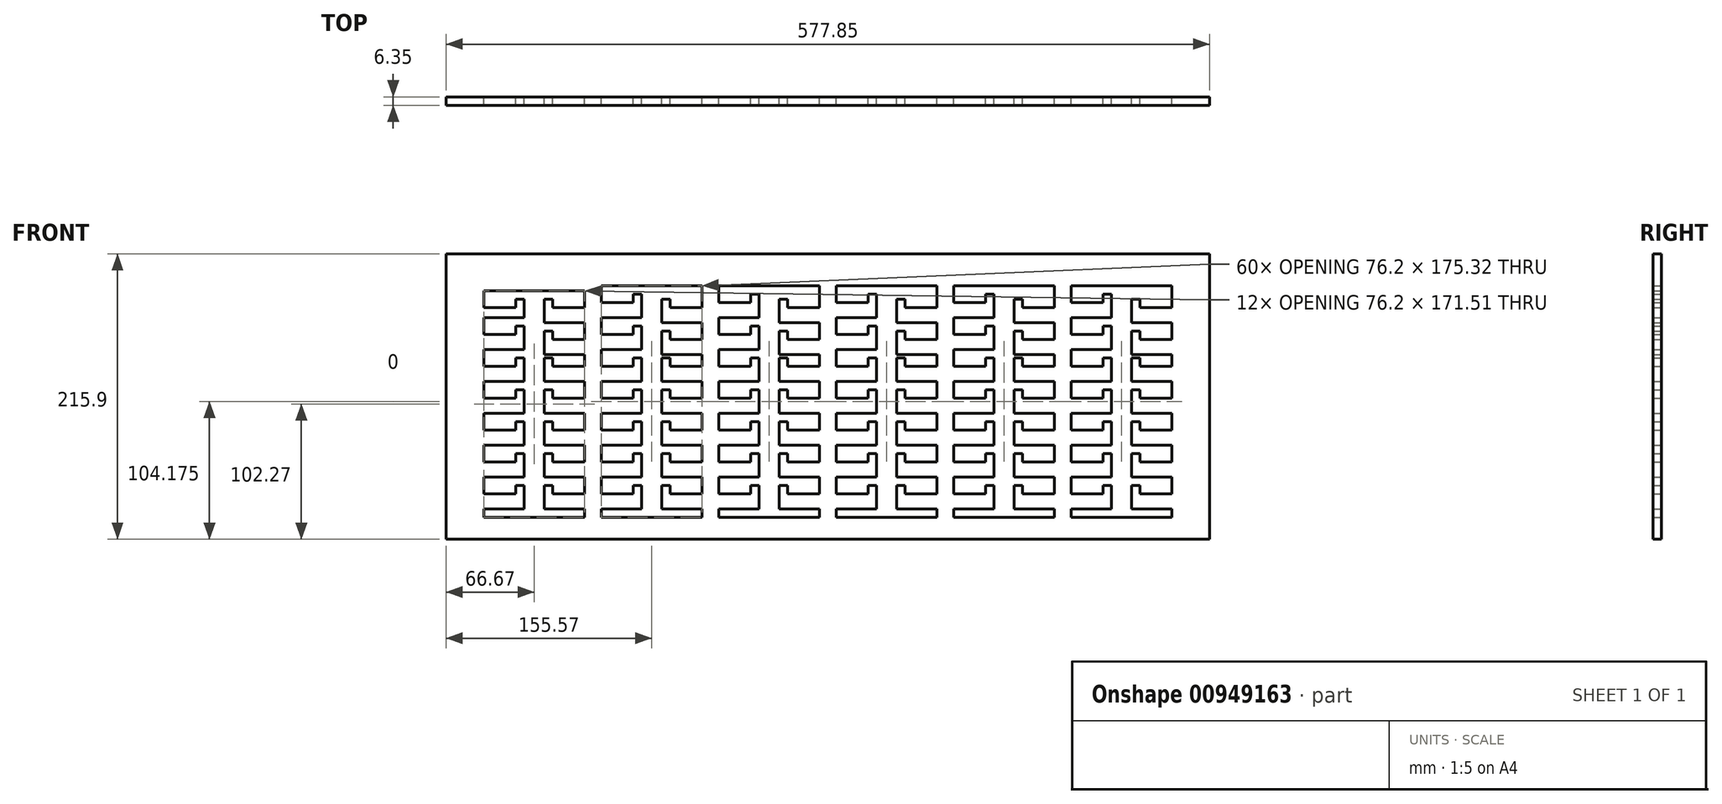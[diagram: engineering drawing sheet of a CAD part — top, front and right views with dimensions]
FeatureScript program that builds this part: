
annotation { "Feature Type Name" : "Feature", "Feature Type Description" : "" }
export const myFeature = defineFeature(function(context is Context, id is Id, definition is map)
    precondition{}
    {
        {
            var Q0;
            Q0=qCreatedBy(makeId("Front.planeOp"),FACE);
            var sketch = newSketch(context, id + "F0", { "sketchPlane" : qUnion([Q0])});
            skLineSegment(sketch, "E0", {"start": v(-97.96, -45.7) * mm, "end": v(-67.48, -45.7) * mm});
            skLineSegment(sketch, "E1", {"start": v(-67.48, -45.7) * mm, "end": v(-67.48, -27.91) * mm});
            skLineSegment(sketch, "E2", {"start": v(-67.48, -27.91) * mm, "end": v(-73.83, -27.91) * mm});
            skLineSegment(sketch, "E3", {"start": v(-73.83, -27.91) * mm, "end": v(-73.83, -34.26) * mm});
            skLineSegment(sketch, "E4", {"start": v(-73.83, -34.26) * mm, "end": v(-97.96, -34.26) * mm});
            skLineSegment(sketch, "E5", {"start": v(-97.96, -34.26) * mm, "end": v(-97.96, -21.56) * mm});
            skLineSegment(sketch, "E6", {"start": v(-97.96, -21.56) * mm, "end": v(-67.48, -21.56) * mm});
            skLineSegment(sketch, "E7", {"start": v(-67.48, -21.56) * mm, "end": v(-67.48, -3.78) * mm});
            skLineSegment(sketch, "E8", {"start": v(-67.48, -3.78) * mm, "end": v(-73.83, -3.78) * mm});
            skLineSegment(sketch, "E9", {"start": v(-73.83, -3.78) * mm, "end": v(-73.83, -10.13) * mm});
            skLineSegment(sketch, "E10", {"start": v(-73.83, -10.13) * mm, "end": v(-97.96, -10.13) * mm});
            skLineSegment(sketch, "E11", {"start": v(-97.96, -10.13) * mm, "end": v(-97.96, 2.57) * mm});
            skLineSegment(sketch, "E12", {"start": v(-97.96, 2.57) * mm, "end": v(-67.48, 2.57) * mm});
            skLineSegment(sketch, "E13", {"start": v(-67.48, 2.57) * mm, "end": v(-67.48, 20.35) * mm});
            skLineSegment(sketch, "E14", {"start": v(-67.48, 20.35) * mm, "end": v(-73.83, 20.35) * mm});
            skLineSegment(sketch, "E15", {"start": v(-73.83, 20.35) * mm, "end": v(-73.83, 14) * mm});
            skLineSegment(sketch, "E16", {"start": v(-73.83, 14) * mm, "end": v(-97.96, 14) * mm});
            skLineSegment(sketch, "E17", {"start": v(-97.96, 14) * mm, "end": v(-97.96, 26.7) * mm});
            skLineSegment(sketch, "E18", {"start": v(-97.96, 26.7) * mm, "end": v(-67.48, 26.7) * mm});
            skLineSegment(sketch, "E19", {"start": v(-67.48, 26.7) * mm, "end": v(-67.48, 44.48) * mm});
            skLineSegment(sketch, "E20", {"start": v(-67.48, 44.48) * mm, "end": v(-73.83, 44.48) * mm});
            skLineSegment(sketch, "E21", {"start": v(-73.83, 44.48) * mm, "end": v(-73.83, 38.13) * mm});
            skLineSegment(sketch, "E22", {"start": v(-73.83, 38.13) * mm, "end": v(-97.96, 38.13) * mm});
            skLineSegment(sketch, "E23", {"start": v(-97.96, 38.13) * mm, "end": v(-97.96, 50.83) * mm});
            skLineSegment(sketch, "E24", {"start": v(-21.76, -76.24) * mm, "end": v(-21.76, -69.82) * mm});
            skLineSegment(sketch, "E25", {"start": v(-21.76, -69.82) * mm, "end": v(-52.24, -69.82) * mm});
            skLineSegment(sketch, "E26", {"start": v(-52.24, -69.82) * mm, "end": v(-52.24, -52.04) * mm});
            skLineSegment(sketch, "E27", {"start": v(-52.24, -52.04) * mm, "end": v(-45.89, -52.04) * mm});
            skLineSegment(sketch, "E28", {"start": v(-45.89, -52.04) * mm, "end": v(-45.89, -58.4) * mm});
            skLineSegment(sketch, "E29", {"start": v(-45.89, -58.4) * mm, "end": v(-21.76, -58.4) * mm});
            skLineSegment(sketch, "E30", {"start": v(-21.76, -58.4) * mm, "end": v(-21.76, -45.7) * mm});
            skLineSegment(sketch, "E31", {"start": v(-21.76, -45.7) * mm, "end": v(-52.24, -45.7) * mm});
            skLineSegment(sketch, "E32", {"start": v(-52.24, -45.7) * mm, "end": v(-52.24, -27.91) * mm});
            skLineSegment(sketch, "E33", {"start": v(-52.24, -27.91) * mm, "end": v(-45.89, -27.91) * mm});
            skLineSegment(sketch, "E34", {"start": v(-45.89, -27.91) * mm, "end": v(-45.89, -34.26) * mm});
            skLineSegment(sketch, "E35", {"start": v(-45.89, -34.26) * mm, "end": v(-21.76, -34.26) * mm});
            skLineSegment(sketch, "E36", {"start": v(-21.76, -34.26) * mm, "end": v(-21.76, -21.56) * mm});
            skLineSegment(sketch, "E37", {"start": v(-21.76, -21.56) * mm, "end": v(-52.24, -21.56) * mm});
            skLineSegment(sketch, "E38", {"start": v(-52.24, -21.56) * mm, "end": v(-52.24, -3.78) * mm});
            skLineSegment(sketch, "E39", {"start": v(-52.24, -3.78) * mm, "end": v(-45.89, -3.78) * mm});
            skLineSegment(sketch, "E40", {"start": v(-45.89, -3.78) * mm, "end": v(-45.89, -10.13) * mm});
            skLineSegment(sketch, "E41", {"start": v(-45.89, -10.13) * mm, "end": v(-21.76, -10.13) * mm});
            skLineSegment(sketch, "E42", {"start": v(-21.76, -10.13) * mm, "end": v(-21.76, 2.57) * mm});
            skLineSegment(sketch, "E43", {"start": v(-21.76, 2.57) * mm, "end": v(-52.24, 2.57) * mm});
            skLineSegment(sketch, "E44", {"start": v(-52.24, 2.57) * mm, "end": v(-52.24, 20.35) * mm});
            skLineSegment(sketch, "E45", {"start": v(-52.24, 20.35) * mm, "end": v(-45.89, 20.35) * mm});
            skLineSegment(sketch, "E46", {"start": v(-45.89, 20.35) * mm, "end": v(-45.89, 14) * mm});
            skLineSegment(sketch, "E47", {"start": v(-45.89, 14) * mm, "end": v(-21.76, 14) * mm});
            skLineSegment(sketch, "E48", {"start": v(-21.76, 14) * mm, "end": v(-21.76, 26.7) * mm});
            skLineSegment(sketch, "E49", {"start": v(-21.76, 26.7) * mm, "end": v(-52.24, 26.7) * mm});
            skLineSegment(sketch, "E50", {"start": v(-52.24, 26.7) * mm, "end": v(-52.24, 44.48) * mm});
            skLineSegment(sketch, "E51", {"start": v(-52.24, 44.48) * mm, "end": v(-45.89, 44.48) * mm});
            skLineSegment(sketch, "E52", {"start": v(-45.89, 44.48) * mm, "end": v(-45.89, 38.13) * mm});
            skLineSegment(sketch, "E53", {"start": v(-45.89, 38.13) * mm, "end": v(-21.76, 38.13) * mm});
            skLineSegment(sketch, "E54", {"start": v(-21.76, 38.13) * mm, "end": v(-21.76, 50.83) * mm});
            skLineSegment(sketch, "E55", {"start": v(-67.48, -69.82) * mm, "end": v(-67.48, -52.04) * mm});
            skLineSegment(sketch, "E56", {"start": v(-73.83, -58.4) * mm, "end": v(-73.83, -52.04) * mm});
            skLineSegment(sketch, "E57", {"start": v(-73.83, -52.04) * mm, "end": v(-67.48, -52.04) * mm});
            skLineSegment(sketch, "E58", {"start": v(-67.48, -69.82) * mm, "end": v(-97.96, -69.82) * mm});
            skLineSegment(sketch, "E59", {"start": v(-97.96, -58.4) * mm, "end": v(-97.96, -45.7) * mm});
            skLineSegment(sketch, "E60", {"start": v(-97.96, -69.82) * mm, "end": v(-97.96, -76.24) * mm});
            skLineSegment(sketch, "E61", {"start": v(-97.96, -58.4) * mm, "end": v(-73.83, -58.4) * mm});
            skLineSegment(sketch, "E62", {"start": v(-97.96, -76.24) * mm, "end": v(-21.76, -76.24) * mm});
            skPoint(sketch, "E63", {"position": v(-59.86, -76.24) * mm});
            skLineSegment(sketch, "E64", {"start": v(-186.86, -45.7) * mm, "end": v(-156.38, -45.7) * mm});
            skLineSegment(sketch, "E65", {"start": v(-156.38, -45.7) * mm, "end": v(-156.38, -27.91) * mm});
            skLineSegment(sketch, "E66", {"start": v(-156.38, -27.91) * mm, "end": v(-162.73, -27.91) * mm});
            skLineSegment(sketch, "E67", {"start": v(-162.73, -27.91) * mm, "end": v(-162.73, -34.26) * mm});
            skLineSegment(sketch, "E68", {"start": v(-162.73, -34.26) * mm, "end": v(-186.86, -34.26) * mm});
            skLineSegment(sketch, "E69", {"start": v(-186.86, -34.26) * mm, "end": v(-186.86, -21.56) * mm});
            skLineSegment(sketch, "E70", {"start": v(-186.86, -21.56) * mm, "end": v(-156.38, -21.56) * mm});
            skLineSegment(sketch, "E71", {"start": v(-156.38, -21.56) * mm, "end": v(-156.38, -3.78) * mm});
            skLineSegment(sketch, "E72", {"start": v(-156.38, -3.78) * mm, "end": v(-162.73, -3.78) * mm});
            skLineSegment(sketch, "E73", {"start": v(-162.73, -3.78) * mm, "end": v(-162.73, -10.13) * mm});
            skLineSegment(sketch, "E74", {"start": v(-162.73, -10.13) * mm, "end": v(-186.86, -10.13) * mm});
            skLineSegment(sketch, "E75", {"start": v(-186.86, -10.13) * mm, "end": v(-186.86, 2.57) * mm});
            skLineSegment(sketch, "E76", {"start": v(-186.86, 2.57) * mm, "end": v(-156.38, 2.57) * mm});
            skLineSegment(sketch, "E77", {"start": v(-156.38, 2.57) * mm, "end": v(-156.38, 20.35) * mm});
            skLineSegment(sketch, "E78", {"start": v(-156.38, 20.35) * mm, "end": v(-162.73, 20.35) * mm});
            skLineSegment(sketch, "E79", {"start": v(-162.73, 20.35) * mm, "end": v(-162.73, 14) * mm});
            skLineSegment(sketch, "E80", {"start": v(-162.73, 14) * mm, "end": v(-186.86, 14) * mm});
            skLineSegment(sketch, "E81", {"start": v(-186.86, 14) * mm, "end": v(-186.86, 26.7) * mm});
            skLineSegment(sketch, "E82", {"start": v(-186.86, 26.7) * mm, "end": v(-156.38, 26.7) * mm});
            skLineSegment(sketch, "E83", {"start": v(-156.38, 26.7) * mm, "end": v(-156.38, 44.48) * mm});
            skLineSegment(sketch, "E84", {"start": v(-156.38, 44.48) * mm, "end": v(-162.73, 44.48) * mm});
            skLineSegment(sketch, "E85", {"start": v(-162.73, 44.48) * mm, "end": v(-162.73, 38.13) * mm});
            skLineSegment(sketch, "E86", {"start": v(-162.73, 38.13) * mm, "end": v(-186.86, 38.13) * mm});
            skLineSegment(sketch, "E87", {"start": v(-186.86, 38.13) * mm, "end": v(-186.86, 50.83) * mm});
            skLineSegment(sketch, "E88", {"start": v(-110.66, -76.24) * mm, "end": v(-110.66, -69.82) * mm});
            skLineSegment(sketch, "E89", {"start": v(-110.66, -69.82) * mm, "end": v(-141.14, -69.82) * mm});
            skLineSegment(sketch, "E90", {"start": v(-141.14, -69.82) * mm, "end": v(-141.14, -52.04) * mm});
            skLineSegment(sketch, "E91", {"start": v(-141.14, -52.04) * mm, "end": v(-134.79, -52.04) * mm});
            skLineSegment(sketch, "E92", {"start": v(-134.79, -52.04) * mm, "end": v(-134.79, -58.4) * mm});
            skLineSegment(sketch, "E93", {"start": v(-134.79, -58.4) * mm, "end": v(-110.66, -58.4) * mm});
            skLineSegment(sketch, "E94", {"start": v(-110.66, -58.4) * mm, "end": v(-110.66, -45.7) * mm});
            skLineSegment(sketch, "E95", {"start": v(-110.66, -45.7) * mm, "end": v(-141.14, -45.7) * mm});
            skLineSegment(sketch, "E96", {"start": v(-141.14, -45.7) * mm, "end": v(-141.14, -27.91) * mm});
            skLineSegment(sketch, "E97", {"start": v(-141.14, -27.91) * mm, "end": v(-134.79, -27.91) * mm});
            skLineSegment(sketch, "E98", {"start": v(-134.79, -27.91) * mm, "end": v(-134.79, -34.26) * mm});
            skLineSegment(sketch, "E99", {"start": v(-134.79, -34.26) * mm, "end": v(-110.66, -34.26) * mm});
            skLineSegment(sketch, "E100", {"start": v(-110.66, -34.26) * mm, "end": v(-110.66, -21.56) * mm});
            skLineSegment(sketch, "E101", {"start": v(-110.66, -21.56) * mm, "end": v(-141.14, -21.56) * mm});
            skLineSegment(sketch, "E102", {"start": v(-141.14, -21.56) * mm, "end": v(-141.14, -3.78) * mm});
            skLineSegment(sketch, "E103", {"start": v(-141.14, -3.78) * mm, "end": v(-134.79, -3.78) * mm});
            skLineSegment(sketch, "E104", {"start": v(-134.79, -3.78) * mm, "end": v(-134.79, -10.13) * mm});
            skLineSegment(sketch, "E105", {"start": v(-134.79, -10.13) * mm, "end": v(-110.66, -10.13) * mm});
            skLineSegment(sketch, "E106", {"start": v(-110.66, -10.13) * mm, "end": v(-110.66, 2.57) * mm});
            skLineSegment(sketch, "E107", {"start": v(-110.66, 2.57) * mm, "end": v(-141.14, 2.57) * mm});
            skLineSegment(sketch, "E108", {"start": v(-141.14, 2.57) * mm, "end": v(-141.14, 20.35) * mm});
            skLineSegment(sketch, "E109", {"start": v(-141.14, 20.35) * mm, "end": v(-134.79, 20.35) * mm});
            skLineSegment(sketch, "E110", {"start": v(-134.79, 20.35) * mm, "end": v(-134.79, 14) * mm});
            skLineSegment(sketch, "E111", {"start": v(-134.79, 14) * mm, "end": v(-110.66, 14) * mm});
            skLineSegment(sketch, "E112", {"start": v(-110.66, 14) * mm, "end": v(-110.66, 26.7) * mm});
            skLineSegment(sketch, "E113", {"start": v(-110.66, 26.7) * mm, "end": v(-141.14, 26.7) * mm});
            skLineSegment(sketch, "E114", {"start": v(-141.14, 26.7) * mm, "end": v(-141.14, 44.48) * mm});
            skLineSegment(sketch, "E115", {"start": v(-141.14, 44.48) * mm, "end": v(-134.79, 44.48) * mm});
            skLineSegment(sketch, "E116", {"start": v(-134.79, 44.48) * mm, "end": v(-134.79, 38.13) * mm});
            skLineSegment(sketch, "E117", {"start": v(-134.79, 38.13) * mm, "end": v(-110.66, 38.13) * mm});
            skLineSegment(sketch, "E118", {"start": v(-110.66, 38.13) * mm, "end": v(-110.66, 50.83) * mm});
            skLineSegment(sketch, "E119", {"start": v(-156.38, -69.82) * mm, "end": v(-156.38, -52.04) * mm});
            skLineSegment(sketch, "E120", {"start": v(-162.73, -58.4) * mm, "end": v(-162.73, -52.04) * mm});
            skLineSegment(sketch, "E121", {"start": v(-162.73, -52.04) * mm, "end": v(-156.38, -52.04) * mm});
            skLineSegment(sketch, "E122", {"start": v(-156.38, -69.82) * mm, "end": v(-186.86, -69.82) * mm});
            skLineSegment(sketch, "E123", {"start": v(-186.86, -58.4) * mm, "end": v(-186.86, -45.7) * mm});
            skLineSegment(sketch, "E124", {"start": v(-186.86, -69.82) * mm, "end": v(-186.86, -76.24) * mm});
            skLineSegment(sketch, "E125", {"start": v(-186.86, -58.4) * mm, "end": v(-162.73, -58.4) * mm});
            skLineSegment(sketch, "E126", {"start": v(-186.86, -76.24) * mm, "end": v(-110.66, -76.24) * mm});
            skPoint(sketch, "E127", {"position": v(-148.76, -76.24) * mm});
            skLineSegment(sketch, "E128", {"start": v(-275.76, -45.7) * mm, "end": v(-245.28, -45.7) * mm});
            skLineSegment(sketch, "E129", {"start": v(-245.28, -45.7) * mm, "end": v(-245.28, -27.91) * mm});
            skLineSegment(sketch, "E130", {"start": v(-245.28, -27.91) * mm, "end": v(-251.63, -27.91) * mm});
            skLineSegment(sketch, "E131", {"start": v(-251.63, -27.91) * mm, "end": v(-251.63, -34.26) * mm});
            skLineSegment(sketch, "E132", {"start": v(-251.63, -34.26) * mm, "end": v(-275.76, -34.26) * mm});
            skLineSegment(sketch, "E133", {"start": v(-275.76, -34.26) * mm, "end": v(-275.76, -21.56) * mm});
            skLineSegment(sketch, "E134", {"start": v(-275.76, -21.56) * mm, "end": v(-245.28, -21.56) * mm});
            skLineSegment(sketch, "E135", {"start": v(-245.28, -21.56) * mm, "end": v(-245.28, -3.78) * mm});
            skLineSegment(sketch, "E136", {"start": v(-245.28, -3.78) * mm, "end": v(-251.63, -3.78) * mm});
            skLineSegment(sketch, "E137", {"start": v(-251.63, -3.78) * mm, "end": v(-251.63, -10.13) * mm});
            skLineSegment(sketch, "E138", {"start": v(-251.63, -10.13) * mm, "end": v(-275.76, -10.13) * mm});
            skLineSegment(sketch, "E139", {"start": v(-275.76, -10.13) * mm, "end": v(-275.76, 2.57) * mm});
            skLineSegment(sketch, "E140", {"start": v(-275.76, 2.57) * mm, "end": v(-245.28, 2.57) * mm});
            skLineSegment(sketch, "E141", {"start": v(-245.28, 2.57) * mm, "end": v(-245.28, 20.35) * mm});
            skLineSegment(sketch, "E142", {"start": v(-245.28, 20.35) * mm, "end": v(-251.63, 20.35) * mm});
            skLineSegment(sketch, "E143", {"start": v(-251.63, 20.35) * mm, "end": v(-251.63, 14) * mm});
            skLineSegment(sketch, "E144", {"start": v(-251.63, 14) * mm, "end": v(-275.76, 14) * mm});
            skLineSegment(sketch, "E145", {"start": v(-275.76, 14) * mm, "end": v(-275.76, 26.7) * mm});
            skLineSegment(sketch, "E146", {"start": v(-275.76, 26.7) * mm, "end": v(-245.28, 26.7) * mm});
            skLineSegment(sketch, "E147", {"start": v(-245.28, 26.7) * mm, "end": v(-245.28, 44.48) * mm});
            skLineSegment(sketch, "E148", {"start": v(-245.28, 44.48) * mm, "end": v(-251.63, 44.48) * mm});
            skLineSegment(sketch, "E149", {"start": v(-251.63, 44.48) * mm, "end": v(-251.63, 38.13) * mm});
            skLineSegment(sketch, "E150", {"start": v(-251.63, 38.13) * mm, "end": v(-275.76, 38.13) * mm});
            skLineSegment(sketch, "E151", {"start": v(-275.76, 38.13) * mm, "end": v(-275.76, 50.83) * mm});
            skLineSegment(sketch, "E152", {"start": v(-199.56, -76.24) * mm, "end": v(-199.56, -69.82) * mm});
            skLineSegment(sketch, "E153", {"start": v(-199.56, -69.82) * mm, "end": v(-230.04, -69.82) * mm});
            skLineSegment(sketch, "E154", {"start": v(-230.04, -69.82) * mm, "end": v(-230.04, -52.04) * mm});
            skLineSegment(sketch, "E155", {"start": v(-230.04, -52.04) * mm, "end": v(-223.69, -52.04) * mm});
            skLineSegment(sketch, "E156", {"start": v(-223.69, -52.04) * mm, "end": v(-223.69, -58.4) * mm});
            skLineSegment(sketch, "E157", {"start": v(-223.69, -58.4) * mm, "end": v(-199.56, -58.4) * mm});
            skLineSegment(sketch, "E158", {"start": v(-199.56, -58.4) * mm, "end": v(-199.56, -45.7) * mm});
            skLineSegment(sketch, "E159", {"start": v(-199.56, -45.7) * mm, "end": v(-230.04, -45.7) * mm});
            skLineSegment(sketch, "E160", {"start": v(-230.04, -45.7) * mm, "end": v(-230.04, -27.91) * mm});
            skLineSegment(sketch, "E161", {"start": v(-230.04, -27.91) * mm, "end": v(-223.69, -27.91) * mm});
            skLineSegment(sketch, "E162", {"start": v(-223.69, -27.91) * mm, "end": v(-223.69, -34.26) * mm});
            skLineSegment(sketch, "E163", {"start": v(-223.69, -34.26) * mm, "end": v(-199.56, -34.26) * mm});
            skLineSegment(sketch, "E164", {"start": v(-199.56, -34.26) * mm, "end": v(-199.56, -21.56) * mm});
            skLineSegment(sketch, "E165", {"start": v(-199.56, -21.56) * mm, "end": v(-230.04, -21.56) * mm});
            skLineSegment(sketch, "E166", {"start": v(-230.04, -21.56) * mm, "end": v(-230.04, -3.78) * mm});
            skLineSegment(sketch, "E167", {"start": v(-230.04, -3.78) * mm, "end": v(-223.69, -3.78) * mm});
            skLineSegment(sketch, "E168", {"start": v(-223.69, -3.78) * mm, "end": v(-223.69, -10.13) * mm});
            skLineSegment(sketch, "E169", {"start": v(-223.69, -10.13) * mm, "end": v(-199.56, -10.13) * mm});
            skLineSegment(sketch, "E170", {"start": v(-199.56, -10.13) * mm, "end": v(-199.56, 2.57) * mm});
            skLineSegment(sketch, "E171", {"start": v(-199.56, 2.57) * mm, "end": v(-230.04, 2.57) * mm});
            skLineSegment(sketch, "E172", {"start": v(-230.04, 2.57) * mm, "end": v(-230.04, 20.35) * mm});
            skLineSegment(sketch, "E173", {"start": v(-230.04, 20.35) * mm, "end": v(-223.69, 20.35) * mm});
            skLineSegment(sketch, "E174", {"start": v(-223.69, 20.35) * mm, "end": v(-223.69, 14) * mm});
            skLineSegment(sketch, "E175", {"start": v(-223.69, 14) * mm, "end": v(-199.56, 14) * mm});
            skLineSegment(sketch, "E176", {"start": v(-199.56, 14) * mm, "end": v(-199.56, 26.7) * mm});
            skLineSegment(sketch, "E177", {"start": v(-199.56, 26.7) * mm, "end": v(-230.04, 26.7) * mm});
            skLineSegment(sketch, "E178", {"start": v(-230.04, 26.7) * mm, "end": v(-230.04, 44.48) * mm});
            skLineSegment(sketch, "E179", {"start": v(-230.04, 44.48) * mm, "end": v(-223.69, 44.48) * mm});
            skLineSegment(sketch, "E180", {"start": v(-223.69, 44.48) * mm, "end": v(-223.69, 38.13) * mm});
            skLineSegment(sketch, "E181", {"start": v(-223.69, 38.13) * mm, "end": v(-199.56, 38.13) * mm});
            skLineSegment(sketch, "E182", {"start": v(-199.56, 38.13) * mm, "end": v(-199.56, 50.83) * mm});
            skLineSegment(sketch, "E183", {"start": v(-245.28, -69.82) * mm, "end": v(-245.28, -52.04) * mm});
            skLineSegment(sketch, "E184", {"start": v(-251.63, -58.4) * mm, "end": v(-251.63, -52.04) * mm});
            skLineSegment(sketch, "E185", {"start": v(-251.63, -52.04) * mm, "end": v(-245.28, -52.04) * mm});
            skLineSegment(sketch, "E186", {"start": v(-245.28, -69.82) * mm, "end": v(-275.76, -69.82) * mm});
            skLineSegment(sketch, "E187", {"start": v(-275.76, -58.4) * mm, "end": v(-275.76, -45.7) * mm});
            skLineSegment(sketch, "E188", {"start": v(-275.76, -69.82) * mm, "end": v(-275.76, -76.24) * mm});
            skLineSegment(sketch, "E189", {"start": v(-275.76, -58.4) * mm, "end": v(-251.63, -58.4) * mm});
            skLineSegment(sketch, "E190", {"start": v(-275.76, -76.24) * mm, "end": v(-199.56, -76.24) * mm});
            skPoint(sketch, "E191", {"position": v(-237.66, -76.24) * mm});
            skLineSegment(sketch, "E192", {"start": v(-364.66, -45.7) * mm, "end": v(-334.18, -45.7) * mm});
            skLineSegment(sketch, "E193", {"start": v(-334.18, -45.7) * mm, "end": v(-334.18, -27.91) * mm});
            skLineSegment(sketch, "E194", {"start": v(-334.18, -27.91) * mm, "end": v(-340.53, -27.91) * mm});
            skLineSegment(sketch, "E195", {"start": v(-340.53, -27.91) * mm, "end": v(-340.53, -34.26) * mm});
            skLineSegment(sketch, "E196", {"start": v(-340.53, -34.26) * mm, "end": v(-364.66, -34.26) * mm});
            skLineSegment(sketch, "E197", {"start": v(-364.66, -34.26) * mm, "end": v(-364.66, -21.56) * mm});
            skLineSegment(sketch, "E198", {"start": v(-364.66, -21.56) * mm, "end": v(-334.18, -21.56) * mm});
            skLineSegment(sketch, "E199", {"start": v(-334.18, -21.56) * mm, "end": v(-334.18, -3.78) * mm});
            skLineSegment(sketch, "E200", {"start": v(-334.18, -3.78) * mm, "end": v(-340.53, -3.78) * mm});
            skLineSegment(sketch, "E201", {"start": v(-340.53, -3.78) * mm, "end": v(-340.53, -10.13) * mm});
            skLineSegment(sketch, "E202", {"start": v(-340.53, -10.13) * mm, "end": v(-364.66, -10.13) * mm});
            skLineSegment(sketch, "E203", {"start": v(-364.66, -10.13) * mm, "end": v(-364.66, 2.57) * mm});
            skLineSegment(sketch, "E204", {"start": v(-364.66, 2.57) * mm, "end": v(-334.18, 2.57) * mm});
            skLineSegment(sketch, "E205", {"start": v(-334.18, 2.57) * mm, "end": v(-334.18, 20.35) * mm});
            skLineSegment(sketch, "E206", {"start": v(-334.18, 20.35) * mm, "end": v(-340.53, 20.35) * mm});
            skLineSegment(sketch, "E207", {"start": v(-340.53, 20.35) * mm, "end": v(-340.53, 14) * mm});
            skLineSegment(sketch, "E208", {"start": v(-340.53, 14) * mm, "end": v(-364.66, 14) * mm});
            skLineSegment(sketch, "E209", {"start": v(-364.66, 14) * mm, "end": v(-364.66, 26.7) * mm});
            skLineSegment(sketch, "E210", {"start": v(-364.66, 26.7) * mm, "end": v(-334.18, 26.7) * mm});
            skLineSegment(sketch, "E211", {"start": v(-334.18, 26.7) * mm, "end": v(-334.18, 44.48) * mm});
            skLineSegment(sketch, "E212", {"start": v(-334.18, 44.48) * mm, "end": v(-340.53, 44.48) * mm});
            skLineSegment(sketch, "E213", {"start": v(-340.53, 44.48) * mm, "end": v(-340.53, 38.13) * mm});
            skLineSegment(sketch, "E214", {"start": v(-340.53, 38.13) * mm, "end": v(-364.66, 38.13) * mm});
            skLineSegment(sketch, "E215", {"start": v(-364.66, 38.13) * mm, "end": v(-364.66, 50.83) * mm});
            skLineSegment(sketch, "E216", {"start": v(-288.46, -76.24) * mm, "end": v(-288.46, -69.82) * mm});
            skLineSegment(sketch, "E217", {"start": v(-288.46, -69.82) * mm, "end": v(-318.94, -69.82) * mm});
            skLineSegment(sketch, "E218", {"start": v(-318.94, -69.82) * mm, "end": v(-318.94, -52.04) * mm});
            skLineSegment(sketch, "E219", {"start": v(-318.94, -52.04) * mm, "end": v(-312.59, -52.04) * mm});
            skLineSegment(sketch, "E220", {"start": v(-312.59, -52.04) * mm, "end": v(-312.59, -58.4) * mm});
            skLineSegment(sketch, "E221", {"start": v(-312.59, -58.4) * mm, "end": v(-288.46, -58.4) * mm});
            skLineSegment(sketch, "E222", {"start": v(-288.46, -58.4) * mm, "end": v(-288.46, -45.7) * mm});
            skLineSegment(sketch, "E223", {"start": v(-288.46, -45.7) * mm, "end": v(-318.94, -45.7) * mm});
            skLineSegment(sketch, "E224", {"start": v(-318.94, -45.7) * mm, "end": v(-318.94, -27.91) * mm});
            skLineSegment(sketch, "E225", {"start": v(-318.94, -27.91) * mm, "end": v(-312.59, -27.91) * mm});
            skLineSegment(sketch, "E226", {"start": v(-312.59, -27.91) * mm, "end": v(-312.59, -34.26) * mm});
            skLineSegment(sketch, "E227", {"start": v(-312.59, -34.26) * mm, "end": v(-288.46, -34.26) * mm});
            skLineSegment(sketch, "E228", {"start": v(-288.46, -34.26) * mm, "end": v(-288.46, -21.56) * mm});
            skLineSegment(sketch, "E229", {"start": v(-288.46, -21.56) * mm, "end": v(-318.94, -21.56) * mm});
            skLineSegment(sketch, "E230", {"start": v(-318.94, -21.56) * mm, "end": v(-318.94, -3.78) * mm});
            skLineSegment(sketch, "E231", {"start": v(-318.94, -3.78) * mm, "end": v(-312.59, -3.78) * mm});
            skLineSegment(sketch, "E232", {"start": v(-312.59, -3.78) * mm, "end": v(-312.59, -10.13) * mm});
            skLineSegment(sketch, "E233", {"start": v(-312.59, -10.13) * mm, "end": v(-288.46, -10.13) * mm});
            skLineSegment(sketch, "E234", {"start": v(-288.46, -10.13) * mm, "end": v(-288.46, 2.57) * mm});
            skLineSegment(sketch, "E235", {"start": v(-288.46, 2.57) * mm, "end": v(-318.94, 2.57) * mm});
            skLineSegment(sketch, "E236", {"start": v(-318.94, 2.57) * mm, "end": v(-318.94, 20.35) * mm});
            skLineSegment(sketch, "E237", {"start": v(-318.94, 20.35) * mm, "end": v(-312.59, 20.35) * mm});
            skLineSegment(sketch, "E238", {"start": v(-312.59, 20.35) * mm, "end": v(-312.59, 14) * mm});
            skLineSegment(sketch, "E239", {"start": v(-312.59, 14) * mm, "end": v(-288.46, 14) * mm});
            skLineSegment(sketch, "E240", {"start": v(-288.46, 14) * mm, "end": v(-288.46, 26.7) * mm});
            skLineSegment(sketch, "E241", {"start": v(-288.46, 26.7) * mm, "end": v(-318.94, 26.7) * mm});
            skLineSegment(sketch, "E242", {"start": v(-318.94, 26.7) * mm, "end": v(-318.94, 44.48) * mm});
            skLineSegment(sketch, "E243", {"start": v(-318.94, 44.48) * mm, "end": v(-312.59, 44.48) * mm});
            skLineSegment(sketch, "E244", {"start": v(-312.59, 44.48) * mm, "end": v(-312.59, 38.13) * mm});
            skLineSegment(sketch, "E245", {"start": v(-312.59, 38.13) * mm, "end": v(-288.46, 38.13) * mm});
            skLineSegment(sketch, "E246", {"start": v(-288.46, 38.13) * mm, "end": v(-288.46, 50.83) * mm});
            skLineSegment(sketch, "E247", {"start": v(-334.18, -69.82) * mm, "end": v(-334.18, -52.04) * mm});
            skLineSegment(sketch, "E248", {"start": v(-340.53, -58.4) * mm, "end": v(-340.53, -52.04) * mm});
            skLineSegment(sketch, "E249", {"start": v(-340.53, -52.04) * mm, "end": v(-334.18, -52.04) * mm});
            skLineSegment(sketch, "E250", {"start": v(-334.18, -69.82) * mm, "end": v(-364.66, -69.82) * mm});
            skLineSegment(sketch, "E251", {"start": v(-364.66, -58.4) * mm, "end": v(-364.66, -45.7) * mm});
            skLineSegment(sketch, "E252", {"start": v(-364.66, -69.82) * mm, "end": v(-364.66, -76.24) * mm});
            skLineSegment(sketch, "E253", {"start": v(-364.66, -58.4) * mm, "end": v(-340.53, -58.4) * mm});
            skLineSegment(sketch, "E254", {"start": v(-364.66, -76.24) * mm, "end": v(-288.46, -76.24) * mm});
            skPoint(sketch, "E255", {"position": v(-326.56, -76.24) * mm});
            skLineSegment(sketch, "E256.bottom", {"start": v(6.82, 123.15) * mm, "end": v(-571.03, 123.15) * mm});
            skLineSegment(sketch, "E256.top", {"start": v(6.82, -92.75) * mm, "end": v(-571.03, -92.75) * mm});
            skLineSegment(sketch, "E256.left", {"start": v(6.82, 123.15) * mm, "end": v(6.82, -92.75) * mm});
            skLineSegment(sketch, "E256.right", {"start": v(-571.03, 123.15) * mm, "end": v(-571.03, -92.75) * mm});
            skPoint(sketch, "E257", {"position": v(-282.1, 123.15) * mm});
            skLineSegment(sketch, "E258", {"start": v(-453.56, -45.7) * mm, "end": v(-423.08, -45.7) * mm});
            skLineSegment(sketch, "E259", {"start": v(-423.08, -45.7) * mm, "end": v(-423.08, -27.91) * mm});
            skLineSegment(sketch, "E260", {"start": v(-423.08, -27.91) * mm, "end": v(-429.43, -27.91) * mm});
            skLineSegment(sketch, "E261", {"start": v(-429.43, -27.91) * mm, "end": v(-429.43, -34.26) * mm});
            skLineSegment(sketch, "E262", {"start": v(-429.43, -34.26) * mm, "end": v(-453.56, -34.26) * mm});
            skLineSegment(sketch, "E263", {"start": v(-453.56, -34.26) * mm, "end": v(-453.56, -21.56) * mm});
            skLineSegment(sketch, "E264", {"start": v(-453.56, -21.56) * mm, "end": v(-423.08, -21.56) * mm});
            skLineSegment(sketch, "E265", {"start": v(-423.08, -21.56) * mm, "end": v(-423.08, -3.78) * mm});
            skLineSegment(sketch, "E266", {"start": v(-423.08, -3.78) * mm, "end": v(-429.43, -3.78) * mm});
            skLineSegment(sketch, "E267", {"start": v(-429.43, -3.78) * mm, "end": v(-429.43, -10.13) * mm});
            skLineSegment(sketch, "E268", {"start": v(-429.43, -10.13) * mm, "end": v(-453.56, -10.13) * mm});
            skLineSegment(sketch, "E269", {"start": v(-453.56, -10.13) * mm, "end": v(-453.56, 2.57) * mm});
            skLineSegment(sketch, "E270", {"start": v(-453.56, 2.57) * mm, "end": v(-423.08, 2.57) * mm});
            skLineSegment(sketch, "E271", {"start": v(-423.08, 2.57) * mm, "end": v(-423.08, 20.35) * mm});
            skLineSegment(sketch, "E272", {"start": v(-423.08, 20.35) * mm, "end": v(-429.43, 20.35) * mm});
            skLineSegment(sketch, "E273", {"start": v(-429.43, 20.35) * mm, "end": v(-429.43, 14) * mm});
            skLineSegment(sketch, "E274", {"start": v(-429.43, 14) * mm, "end": v(-453.56, 14) * mm});
            skLineSegment(sketch, "E275", {"start": v(-453.56, 14) * mm, "end": v(-453.56, 26.7) * mm});
            skLineSegment(sketch, "E276", {"start": v(-453.56, 26.7) * mm, "end": v(-423.08, 26.7) * mm});
            skLineSegment(sketch, "E277", {"start": v(-423.08, 26.7) * mm, "end": v(-423.08, 44.48) * mm});
            skLineSegment(sketch, "E278", {"start": v(-423.08, 44.48) * mm, "end": v(-429.43, 44.48) * mm});
            skLineSegment(sketch, "E279", {"start": v(-429.43, 44.48) * mm, "end": v(-429.43, 38.13) * mm});
            skLineSegment(sketch, "E280", {"start": v(-429.43, 38.13) * mm, "end": v(-453.56, 38.13) * mm});
            skLineSegment(sketch, "E281", {"start": v(-453.56, 38.13) * mm, "end": v(-453.56, 50.83) * mm});
            skLineSegment(sketch, "E282", {"start": v(-377.36, -76.24) * mm, "end": v(-377.36, -69.82) * mm});
            skLineSegment(sketch, "E283", {"start": v(-377.36, -69.82) * mm, "end": v(-407.84, -69.82) * mm});
            skLineSegment(sketch, "E284", {"start": v(-407.84, -69.82) * mm, "end": v(-407.84, -52.04) * mm});
            skLineSegment(sketch, "E285", {"start": v(-407.84, -52.04) * mm, "end": v(-401.49, -52.04) * mm});
            skLineSegment(sketch, "E286", {"start": v(-401.49, -52.04) * mm, "end": v(-401.49, -58.4) * mm});
            skLineSegment(sketch, "E287", {"start": v(-401.49, -58.4) * mm, "end": v(-377.36, -58.4) * mm});
            skLineSegment(sketch, "E288", {"start": v(-377.36, -58.4) * mm, "end": v(-377.36, -45.7) * mm});
            skLineSegment(sketch, "E289", {"start": v(-377.36, -45.7) * mm, "end": v(-407.84, -45.7) * mm});
            skLineSegment(sketch, "E290", {"start": v(-407.84, -45.7) * mm, "end": v(-407.84, -27.91) * mm});
            skLineSegment(sketch, "E291", {"start": v(-407.84, -27.91) * mm, "end": v(-401.49, -27.91) * mm});
            skLineSegment(sketch, "E292", {"start": v(-401.49, -27.91) * mm, "end": v(-401.49, -34.26) * mm});
            skLineSegment(sketch, "E293", {"start": v(-401.49, -34.26) * mm, "end": v(-377.36, -34.26) * mm});
            skLineSegment(sketch, "E294", {"start": v(-377.36, -34.26) * mm, "end": v(-377.36, -21.56) * mm});
            skLineSegment(sketch, "E295", {"start": v(-377.36, -21.56) * mm, "end": v(-407.84, -21.56) * mm});
            skLineSegment(sketch, "E296", {"start": v(-407.84, -21.56) * mm, "end": v(-407.84, -3.78) * mm});
            skLineSegment(sketch, "E297", {"start": v(-407.84, -3.78) * mm, "end": v(-401.49, -3.78) * mm});
            skLineSegment(sketch, "E298", {"start": v(-401.49, -3.78) * mm, "end": v(-401.49, -10.13) * mm});
            skLineSegment(sketch, "E299", {"start": v(-401.49, -10.13) * mm, "end": v(-377.36, -10.13) * mm});
            skLineSegment(sketch, "E300", {"start": v(-377.36, -10.13) * mm, "end": v(-377.36, 2.57) * mm});
            skLineSegment(sketch, "E301", {"start": v(-377.36, 2.57) * mm, "end": v(-407.84, 2.57) * mm});
            skLineSegment(sketch, "E302", {"start": v(-407.84, 2.57) * mm, "end": v(-407.84, 20.35) * mm});
            skLineSegment(sketch, "E303", {"start": v(-407.84, 20.35) * mm, "end": v(-401.49, 20.35) * mm});
            skLineSegment(sketch, "E304", {"start": v(-401.49, 20.35) * mm, "end": v(-401.49, 14) * mm});
            skLineSegment(sketch, "E305", {"start": v(-401.49, 14) * mm, "end": v(-377.36, 14) * mm});
            skLineSegment(sketch, "E306", {"start": v(-377.36, 14) * mm, "end": v(-377.36, 26.7) * mm});
            skLineSegment(sketch, "E307", {"start": v(-377.36, 26.7) * mm, "end": v(-407.84, 26.7) * mm});
            skLineSegment(sketch, "E308", {"start": v(-407.84, 26.7) * mm, "end": v(-407.84, 44.48) * mm});
            skLineSegment(sketch, "E309", {"start": v(-407.84, 44.48) * mm, "end": v(-401.49, 44.48) * mm});
            skLineSegment(sketch, "E310", {"start": v(-401.49, 44.48) * mm, "end": v(-401.49, 38.13) * mm});
            skLineSegment(sketch, "E311", {"start": v(-401.49, 38.13) * mm, "end": v(-377.36, 38.13) * mm});
            skLineSegment(sketch, "E312", {"start": v(-377.36, 38.13) * mm, "end": v(-377.36, 50.83) * mm});
            skLineSegment(sketch, "E313", {"start": v(-423.08, -69.82) * mm, "end": v(-423.08, -52.04) * mm});
            skLineSegment(sketch, "E314", {"start": v(-429.43, -58.4) * mm, "end": v(-429.43, -52.04) * mm});
            skLineSegment(sketch, "E315", {"start": v(-429.43, -52.04) * mm, "end": v(-423.08, -52.04) * mm});
            skLineSegment(sketch, "E316", {"start": v(-423.08, -69.82) * mm, "end": v(-453.56, -69.82) * mm});
            skLineSegment(sketch, "E317", {"start": v(-453.56, -58.4) * mm, "end": v(-453.56, -45.7) * mm});
            skLineSegment(sketch, "E318", {"start": v(-453.56, -69.82) * mm, "end": v(-453.56, -76.24) * mm});
            skLineSegment(sketch, "E319", {"start": v(-453.56, -58.4) * mm, "end": v(-429.43, -58.4) * mm});
            skLineSegment(sketch, "E320", {"start": v(-453.56, -76.24) * mm, "end": v(-377.36, -76.24) * mm});
            skPoint(sketch, "E321", {"position": v(-415.46, -76.24) * mm});
            skLineSegment(sketch, "E322", {"start": v(-542.46, -45.7) * mm, "end": v(-511.98, -45.7) * mm});
            skLineSegment(sketch, "E323", {"start": v(-511.98, -45.7) * mm, "end": v(-511.98, -27.91) * mm});
            skLineSegment(sketch, "E324", {"start": v(-511.98, -27.91) * mm, "end": v(-518.33, -27.91) * mm});
            skLineSegment(sketch, "E325", {"start": v(-518.33, -27.91) * mm, "end": v(-518.33, -34.26) * mm});
            skLineSegment(sketch, "E326", {"start": v(-518.33, -34.26) * mm, "end": v(-542.46, -34.26) * mm});
            skLineSegment(sketch, "E327", {"start": v(-542.46, -34.26) * mm, "end": v(-542.46, -21.56) * mm});
            skLineSegment(sketch, "E328", {"start": v(-542.46, -21.56) * mm, "end": v(-511.98, -21.56) * mm});
            skLineSegment(sketch, "E329", {"start": v(-511.98, -21.56) * mm, "end": v(-511.98, -3.78) * mm});
            skLineSegment(sketch, "E330", {"start": v(-511.98, -3.78) * mm, "end": v(-518.33, -3.78) * mm});
            skLineSegment(sketch, "E331", {"start": v(-518.33, -3.78) * mm, "end": v(-518.33, -10.13) * mm});
            skLineSegment(sketch, "E332", {"start": v(-518.33, -10.13) * mm, "end": v(-542.46, -10.13) * mm});
            skLineSegment(sketch, "E333", {"start": v(-542.46, -10.13) * mm, "end": v(-542.46, 2.57) * mm});
            skLineSegment(sketch, "E334", {"start": v(-542.46, 2.57) * mm, "end": v(-511.98, 2.57) * mm});
            skLineSegment(sketch, "E335", {"start": v(-511.98, 2.57) * mm, "end": v(-511.98, 20.35) * mm});
            skLineSegment(sketch, "E336", {"start": v(-511.98, 20.35) * mm, "end": v(-518.33, 20.35) * mm});
            skLineSegment(sketch, "E337", {"start": v(-518.33, 20.35) * mm, "end": v(-518.33, 14) * mm});
            skLineSegment(sketch, "E338", {"start": v(-518.33, 14) * mm, "end": v(-542.46, 14) * mm});
            skLineSegment(sketch, "E339", {"start": v(-542.46, 14) * mm, "end": v(-542.46, 26.7) * mm});
            skLineSegment(sketch, "E340", {"start": v(-542.46, 26.7) * mm, "end": v(-511.98, 26.7) * mm});
            skLineSegment(sketch, "E341", {"start": v(-511.98, 26.7) * mm, "end": v(-511.98, 44.48) * mm});
            skLineSegment(sketch, "E342", {"start": v(-511.98, 44.48) * mm, "end": v(-518.33, 44.48) * mm});
            skLineSegment(sketch, "E343", {"start": v(-518.33, 44.48) * mm, "end": v(-518.33, 38.13) * mm});
            skLineSegment(sketch, "E344", {"start": v(-518.33, 38.13) * mm, "end": v(-542.46, 38.13) * mm});
            skLineSegment(sketch, "E345", {"start": v(-542.46, 38.13) * mm, "end": v(-542.46, 50.83) * mm});
            skLineSegment(sketch, "E346", {"start": v(-466.26, -76.24) * mm, "end": v(-466.26, -69.82) * mm});
            skLineSegment(sketch, "E347", {"start": v(-466.26, -69.82) * mm, "end": v(-496.74, -69.82) * mm});
            skLineSegment(sketch, "E348", {"start": v(-496.74, -69.82) * mm, "end": v(-496.74, -52.04) * mm});
            skLineSegment(sketch, "E349", {"start": v(-496.74, -52.04) * mm, "end": v(-490.39, -52.04) * mm});
            skLineSegment(sketch, "E350", {"start": v(-490.39, -52.04) * mm, "end": v(-490.39, -58.4) * mm});
            skLineSegment(sketch, "E351", {"start": v(-490.39, -58.4) * mm, "end": v(-466.26, -58.4) * mm});
            skLineSegment(sketch, "E352", {"start": v(-466.26, -58.4) * mm, "end": v(-466.26, -45.7) * mm});
            skLineSegment(sketch, "E353", {"start": v(-466.26, -45.7) * mm, "end": v(-496.74, -45.7) * mm});
            skLineSegment(sketch, "E354", {"start": v(-496.74, -45.7) * mm, "end": v(-496.74, -27.91) * mm});
            skLineSegment(sketch, "E355", {"start": v(-496.74, -27.91) * mm, "end": v(-490.39, -27.91) * mm});
            skLineSegment(sketch, "E356", {"start": v(-490.39, -27.91) * mm, "end": v(-490.39, -34.26) * mm});
            skLineSegment(sketch, "E357", {"start": v(-490.39, -34.26) * mm, "end": v(-466.26, -34.26) * mm});
            skLineSegment(sketch, "E358", {"start": v(-466.26, -34.26) * mm, "end": v(-466.26, -21.56) * mm});
            skLineSegment(sketch, "E359", {"start": v(-466.26, -21.56) * mm, "end": v(-496.74, -21.56) * mm});
            skLineSegment(sketch, "E360", {"start": v(-496.74, -21.56) * mm, "end": v(-496.74, -3.78) * mm});
            skLineSegment(sketch, "E361", {"start": v(-496.74, -3.78) * mm, "end": v(-490.39, -3.78) * mm});
            skLineSegment(sketch, "E362", {"start": v(-490.39, -3.78) * mm, "end": v(-490.39, -10.13) * mm});
            skLineSegment(sketch, "E363", {"start": v(-490.39, -10.13) * mm, "end": v(-466.26, -10.13) * mm});
            skLineSegment(sketch, "E364", {"start": v(-466.26, -10.13) * mm, "end": v(-466.26, 2.57) * mm});
            skLineSegment(sketch, "E365", {"start": v(-466.26, 2.57) * mm, "end": v(-496.74, 2.57) * mm});
            skLineSegment(sketch, "E366", {"start": v(-496.74, 2.57) * mm, "end": v(-496.74, 20.35) * mm});
            skLineSegment(sketch, "E367", {"start": v(-496.74, 20.35) * mm, "end": v(-490.39, 20.35) * mm});
            skLineSegment(sketch, "E368", {"start": v(-490.39, 20.35) * mm, "end": v(-490.39, 14) * mm});
            skLineSegment(sketch, "E369", {"start": v(-490.39, 14) * mm, "end": v(-466.26, 14) * mm});
            skLineSegment(sketch, "E370", {"start": v(-466.26, 14) * mm, "end": v(-466.26, 26.7) * mm});
            skLineSegment(sketch, "E371", {"start": v(-466.26, 26.7) * mm, "end": v(-496.74, 26.7) * mm});
            skLineSegment(sketch, "E372", {"start": v(-496.74, 26.7) * mm, "end": v(-496.74, 44.48) * mm});
            skLineSegment(sketch, "E373", {"start": v(-496.74, 44.48) * mm, "end": v(-490.39, 44.48) * mm});
            skLineSegment(sketch, "E374", {"start": v(-490.39, 44.48) * mm, "end": v(-490.39, 38.13) * mm});
            skLineSegment(sketch, "E375", {"start": v(-490.39, 38.13) * mm, "end": v(-466.26, 38.13) * mm});
            skLineSegment(sketch, "E376", {"start": v(-466.26, 38.13) * mm, "end": v(-466.26, 50.83) * mm});
            skLineSegment(sketch, "E377", {"start": v(-511.98, -69.82) * mm, "end": v(-511.98, -52.04) * mm});
            skLineSegment(sketch, "E378", {"start": v(-518.33, -58.4) * mm, "end": v(-518.33, -52.04) * mm});
            skLineSegment(sketch, "E379", {"start": v(-518.33, -52.04) * mm, "end": v(-511.98, -52.04) * mm});
            skLineSegment(sketch, "E380", {"start": v(-511.98, -69.82) * mm, "end": v(-542.46, -69.82) * mm});
            skLineSegment(sketch, "E381", {"start": v(-542.46, -58.4) * mm, "end": v(-542.46, -45.7) * mm});
            skLineSegment(sketch, "E382", {"start": v(-542.46, -69.82) * mm, "end": v(-542.46, -76.24) * mm});
            skLineSegment(sketch, "E383", {"start": v(-542.46, -58.4) * mm, "end": v(-518.33, -58.4) * mm});
            skLineSegment(sketch, "E384", {"start": v(-542.46, -76.24) * mm, "end": v(-466.26, -76.24) * mm});
            skPoint(sketch, "E385", {"position": v(-504.36, -76.24) * mm});
            skLineSegment(sketch, "E386", {"start": v(-542.46, 50.83) * mm, "end": v(-511.98, 50.83) * mm});
            skLineSegment(sketch, "E387", {"start": v(-511.98, 50.83) * mm, "end": v(-511.98, 68.6) * mm});
            skLineSegment(sketch, "E388", {"start": v(-511.98, 68.6) * mm, "end": v(-518.33, 68.6) * mm});
            skLineSegment(sketch, "E389", {"start": v(-518.33, 68.6) * mm, "end": v(-518.33, 62.26) * mm});
            skLineSegment(sketch, "E390", {"start": v(-518.33, 62.26) * mm, "end": v(-542.46, 62.26) * mm});
            skLineSegment(sketch, "E391", {"start": v(-542.46, 62.26) * mm, "end": v(-542.46, 74.96) * mm});
            skLineSegment(sketch, "E392", {"start": v(-542.46, 74.96) * mm, "end": v(-511.98, 74.96) * mm});
            skLineSegment(sketch, "E393", {"start": v(-511.98, 88.93) * mm, "end": v(-518.33, 88.93) * mm});
            skLineSegment(sketch, "E394", {"start": v(-518.33, 88.93) * mm, "end": v(-518.33, 82.58) * mm});
            skLineSegment(sketch, "E395", {"start": v(-518.33, 82.58) * mm, "end": v(-542.46, 82.58) * mm});
            skLineSegment(sketch, "E396", {"start": v(-542.46, 82.58) * mm, "end": v(-542.46, 95.28) * mm});
            skLineSegment(sketch, "E397", {"start": v(-466.26, 47.02) * mm, "end": v(-496.74, 47.02) * mm});
            skLineSegment(sketch, "E398", {"start": v(-496.74, 47.02) * mm, "end": v(-496.74, 64.8) * mm});
            skLineSegment(sketch, "E399", {"start": v(-496.74, 64.8) * mm, "end": v(-490.39, 64.8) * mm});
            skLineSegment(sketch, "E400", {"start": v(-490.39, 64.8) * mm, "end": v(-490.39, 58.45) * mm});
            skLineSegment(sketch, "E401", {"start": v(-490.39, 58.45) * mm, "end": v(-466.26, 58.45) * mm});
            skLineSegment(sketch, "E402", {"start": v(-466.26, 58.45) * mm, "end": v(-466.26, 71.15) * mm});
            skLineSegment(sketch, "E403", {"start": v(-466.26, 71.15) * mm, "end": v(-496.74, 71.15) * mm});
            skLineSegment(sketch, "E404", {"start": v(-496.74, 71.15) * mm, "end": v(-496.74, 88.93) * mm});
            skLineSegment(sketch, "E405", {"start": v(-496.74, 88.93) * mm, "end": v(-490.39, 88.93) * mm});
            skLineSegment(sketch, "E406", {"start": v(-490.39, 88.93) * mm, "end": v(-490.39, 82.58) * mm});
            skLineSegment(sketch, "E407", {"start": v(-490.39, 82.58) * mm, "end": v(-466.26, 82.58) * mm});
            skLineSegment(sketch, "E408", {"start": v(-466.26, 82.58) * mm, "end": v(-466.26, 95.28) * mm});
            skLineSegment(sketch, "E409", {"start": v(-511.98, 74.96) * mm, "end": v(-511.98, 88.93) * mm});
            skLineSegment(sketch, "E410", {"start": v(-542.46, 95.28) * mm, "end": v(-466.26, 95.28) * mm});
            skPoint(sketch, "E411", {"position": v(-504.36, 95.28) * mm});
            skLineSegment(sketch, "E412", {"start": v(-453.56, 50.83) * mm, "end": v(-423.08, 50.83) * mm});
            skLineSegment(sketch, "E413", {"start": v(-423.08, 50.83) * mm, "end": v(-423.08, 68.6) * mm});
            skLineSegment(sketch, "E414", {"start": v(-423.08, 68.6) * mm, "end": v(-429.43, 68.6) * mm});
            skLineSegment(sketch, "E415", {"start": v(-429.43, 68.6) * mm, "end": v(-429.43, 62.26) * mm});
            skLineSegment(sketch, "E416", {"start": v(-429.43, 62.26) * mm, "end": v(-453.56, 62.26) * mm});
            skLineSegment(sketch, "E417", {"start": v(-453.56, 62.26) * mm, "end": v(-453.56, 74.96) * mm});
            skLineSegment(sketch, "E418", {"start": v(-453.56, 74.96) * mm, "end": v(-423.08, 74.96) * mm});
            skLineSegment(sketch, "E419", {"start": v(-423.08, 92.74) * mm, "end": v(-429.43, 92.74) * mm});
            skLineSegment(sketch, "E420", {"start": v(-429.43, 92.74) * mm, "end": v(-429.43, 86.39) * mm});
            skLineSegment(sketch, "E421", {"start": v(-429.43, 86.39) * mm, "end": v(-453.56, 86.39) * mm});
            skLineSegment(sketch, "E422", {"start": v(-453.56, 86.39) * mm, "end": v(-453.56, 99.09) * mm});
            skLineSegment(sketch, "E423", {"start": v(-377.36, 47.02) * mm, "end": v(-407.84, 47.02) * mm});
            skLineSegment(sketch, "E424", {"start": v(-407.84, 47.02) * mm, "end": v(-407.84, 64.8) * mm});
            skLineSegment(sketch, "E425", {"start": v(-407.84, 64.8) * mm, "end": v(-401.49, 64.8) * mm});
            skLineSegment(sketch, "E426", {"start": v(-401.49, 64.8) * mm, "end": v(-401.49, 58.45) * mm});
            skLineSegment(sketch, "E427", {"start": v(-401.49, 58.45) * mm, "end": v(-377.36, 58.45) * mm});
            skLineSegment(sketch, "E428", {"start": v(-377.36, 58.45) * mm, "end": v(-377.36, 71.15) * mm});
            skLineSegment(sketch, "E429", {"start": v(-377.36, 71.15) * mm, "end": v(-407.84, 71.15) * mm});
            skLineSegment(sketch, "E430", {"start": v(-407.84, 71.15) * mm, "end": v(-407.84, 88.93) * mm});
            skLineSegment(sketch, "E431", {"start": v(-407.84, 88.93) * mm, "end": v(-401.49, 88.93) * mm});
            skLineSegment(sketch, "E432", {"start": v(-401.49, 88.93) * mm, "end": v(-401.49, 82.58) * mm});
            skLineSegment(sketch, "E433", {"start": v(-401.49, 82.58) * mm, "end": v(-377.36, 82.58) * mm});
            skLineSegment(sketch, "E434", {"start": v(-377.36, 82.58) * mm, "end": v(-377.36, 99.09) * mm});
            skLineSegment(sketch, "E435", {"start": v(-423.08, 74.96) * mm, "end": v(-423.08, 92.74) * mm});
            skLineSegment(sketch, "E436", {"start": v(-453.56, 99.09) * mm, "end": v(-377.36, 99.09) * mm});
            skPoint(sketch, "E437", {"position": v(-415.46, 99.09) * mm});
            skLineSegment(sketch, "E438", {"start": v(-364.66, 50.83) * mm, "end": v(-334.18, 50.83) * mm});
            skLineSegment(sketch, "E439", {"start": v(-334.18, 50.83) * mm, "end": v(-334.18, 68.6) * mm});
            skLineSegment(sketch, "E440", {"start": v(-334.18, 68.6) * mm, "end": v(-340.53, 68.6) * mm});
            skLineSegment(sketch, "E441", {"start": v(-340.53, 68.6) * mm, "end": v(-340.53, 62.26) * mm});
            skLineSegment(sketch, "E442", {"start": v(-340.53, 62.26) * mm, "end": v(-364.66, 62.26) * mm});
            skLineSegment(sketch, "E443", {"start": v(-364.66, 62.26) * mm, "end": v(-364.66, 74.96) * mm});
            skLineSegment(sketch, "E444", {"start": v(-364.66, 74.96) * mm, "end": v(-334.18, 74.96) * mm});
            skLineSegment(sketch, "E445", {"start": v(-334.18, 92.74) * mm, "end": v(-340.53, 92.74) * mm});
            skLineSegment(sketch, "E446", {"start": v(-340.53, 92.74) * mm, "end": v(-340.53, 86.39) * mm});
            skLineSegment(sketch, "E447", {"start": v(-340.53, 86.39) * mm, "end": v(-364.66, 86.39) * mm});
            skLineSegment(sketch, "E448", {"start": v(-364.66, 86.39) * mm, "end": v(-364.66, 99.09) * mm});
            skLineSegment(sketch, "E449", {"start": v(-288.46, 47.02) * mm, "end": v(-318.94, 47.02) * mm});
            skLineSegment(sketch, "E450", {"start": v(-318.94, 47.02) * mm, "end": v(-318.94, 64.8) * mm});
            skLineSegment(sketch, "E451", {"start": v(-318.94, 64.8) * mm, "end": v(-312.59, 64.8) * mm});
            skLineSegment(sketch, "E452", {"start": v(-312.59, 64.8) * mm, "end": v(-312.59, 58.45) * mm});
            skLineSegment(sketch, "E453", {"start": v(-312.59, 58.45) * mm, "end": v(-288.46, 58.45) * mm});
            skLineSegment(sketch, "E454", {"start": v(-288.46, 58.45) * mm, "end": v(-288.46, 71.15) * mm});
            skLineSegment(sketch, "E455", {"start": v(-288.46, 71.15) * mm, "end": v(-318.94, 71.15) * mm});
            skLineSegment(sketch, "E456", {"start": v(-318.94, 71.15) * mm, "end": v(-318.94, 88.93) * mm});
            skLineSegment(sketch, "E457", {"start": v(-318.94, 88.93) * mm, "end": v(-312.59, 88.93) * mm});
            skLineSegment(sketch, "E458", {"start": v(-312.59, 88.93) * mm, "end": v(-312.59, 82.58) * mm});
            skLineSegment(sketch, "E459", {"start": v(-312.59, 82.58) * mm, "end": v(-288.46, 82.58) * mm});
            skLineSegment(sketch, "E460", {"start": v(-288.46, 82.58) * mm, "end": v(-288.46, 99.09) * mm});
            skLineSegment(sketch, "E461", {"start": v(-334.18, 74.96) * mm, "end": v(-334.18, 92.74) * mm});
            skLineSegment(sketch, "E462", {"start": v(-364.66, 99.09) * mm, "end": v(-288.46, 99.09) * mm});
            skPoint(sketch, "E463", {"position": v(-326.56, 99.09) * mm});
            skLineSegment(sketch, "E464", {"start": v(-275.76, 50.83) * mm, "end": v(-245.28, 50.83) * mm});
            skLineSegment(sketch, "E465", {"start": v(-245.28, 50.83) * mm, "end": v(-245.28, 68.6) * mm});
            skLineSegment(sketch, "E466", {"start": v(-245.28, 68.6) * mm, "end": v(-251.63, 68.6) * mm});
            skLineSegment(sketch, "E467", {"start": v(-251.63, 68.6) * mm, "end": v(-251.63, 62.26) * mm});
            skLineSegment(sketch, "E468", {"start": v(-251.63, 62.26) * mm, "end": v(-275.76, 62.26) * mm});
            skLineSegment(sketch, "E469", {"start": v(-275.76, 62.26) * mm, "end": v(-275.76, 74.96) * mm});
            skLineSegment(sketch, "E470", {"start": v(-275.76, 74.96) * mm, "end": v(-245.28, 74.96) * mm});
            skLineSegment(sketch, "E471", {"start": v(-245.28, 92.74) * mm, "end": v(-251.63, 92.74) * mm});
            skLineSegment(sketch, "E472", {"start": v(-251.63, 92.74) * mm, "end": v(-251.63, 86.39) * mm});
            skLineSegment(sketch, "E473", {"start": v(-251.63, 86.39) * mm, "end": v(-275.76, 86.39) * mm});
            skLineSegment(sketch, "E474", {"start": v(-275.76, 86.39) * mm, "end": v(-275.76, 99.09) * mm});
            skLineSegment(sketch, "E475", {"start": v(-199.56, 47.02) * mm, "end": v(-230.04, 47.02) * mm});
            skLineSegment(sketch, "E476", {"start": v(-230.04, 47.02) * mm, "end": v(-230.04, 64.8) * mm});
            skLineSegment(sketch, "E477", {"start": v(-230.04, 64.8) * mm, "end": v(-223.69, 64.8) * mm});
            skLineSegment(sketch, "E478", {"start": v(-223.69, 64.8) * mm, "end": v(-223.69, 58.45) * mm});
            skLineSegment(sketch, "E479", {"start": v(-223.69, 58.45) * mm, "end": v(-199.56, 58.45) * mm});
            skLineSegment(sketch, "E480", {"start": v(-199.56, 58.45) * mm, "end": v(-199.56, 71.15) * mm});
            skLineSegment(sketch, "E481", {"start": v(-199.56, 71.15) * mm, "end": v(-230.04, 71.15) * mm});
            skLineSegment(sketch, "E482", {"start": v(-230.04, 71.15) * mm, "end": v(-230.04, 88.93) * mm});
            skLineSegment(sketch, "E483", {"start": v(-230.04, 88.93) * mm, "end": v(-223.69, 88.93) * mm});
            skLineSegment(sketch, "E484", {"start": v(-223.69, 88.93) * mm, "end": v(-223.69, 82.58) * mm});
            skLineSegment(sketch, "E485", {"start": v(-223.69, 82.58) * mm, "end": v(-199.56, 82.58) * mm});
            skLineSegment(sketch, "E486", {"start": v(-199.56, 82.58) * mm, "end": v(-199.56, 99.09) * mm});
            skLineSegment(sketch, "E487", {"start": v(-245.28, 74.96) * mm, "end": v(-245.28, 92.74) * mm});
            skLineSegment(sketch, "E488", {"start": v(-275.76, 99.09) * mm, "end": v(-199.56, 99.09) * mm});
            skPoint(sketch, "E489", {"position": v(-237.66, 99.09) * mm});
            skLineSegment(sketch, "E490", {"start": v(-186.86, 50.83) * mm, "end": v(-156.38, 50.83) * mm});
            skLineSegment(sketch, "E491", {"start": v(-156.38, 50.83) * mm, "end": v(-156.38, 68.6) * mm});
            skLineSegment(sketch, "E492", {"start": v(-156.38, 68.6) * mm, "end": v(-162.73, 68.6) * mm});
            skLineSegment(sketch, "E493", {"start": v(-162.73, 68.6) * mm, "end": v(-162.73, 62.26) * mm});
            skLineSegment(sketch, "E494", {"start": v(-162.73, 62.26) * mm, "end": v(-186.86, 62.26) * mm});
            skLineSegment(sketch, "E495", {"start": v(-186.86, 62.26) * mm, "end": v(-186.86, 74.96) * mm});
            skLineSegment(sketch, "E496", {"start": v(-186.86, 74.96) * mm, "end": v(-156.38, 74.96) * mm});
            skLineSegment(sketch, "E497", {"start": v(-156.38, 92.74) * mm, "end": v(-162.73, 92.74) * mm});
            skLineSegment(sketch, "E498", {"start": v(-162.73, 92.74) * mm, "end": v(-162.73, 86.39) * mm});
            skLineSegment(sketch, "E499", {"start": v(-162.73, 86.39) * mm, "end": v(-186.86, 86.39) * mm});
            skLineSegment(sketch, "E500", {"start": v(-186.86, 86.39) * mm, "end": v(-186.86, 99.09) * mm});
            skLineSegment(sketch, "E501", {"start": v(-110.66, 47.02) * mm, "end": v(-141.14, 47.02) * mm});
            skLineSegment(sketch, "E502", {"start": v(-141.14, 47.02) * mm, "end": v(-141.14, 64.8) * mm});
            skLineSegment(sketch, "E503", {"start": v(-141.14, 64.8) * mm, "end": v(-134.79, 64.8) * mm});
            skLineSegment(sketch, "E504", {"start": v(-134.79, 64.8) * mm, "end": v(-134.79, 58.45) * mm});
            skLineSegment(sketch, "E505", {"start": v(-134.79, 58.45) * mm, "end": v(-110.66, 58.45) * mm});
            skLineSegment(sketch, "E506", {"start": v(-110.66, 58.45) * mm, "end": v(-110.66, 71.15) * mm});
            skLineSegment(sketch, "E507", {"start": v(-110.66, 71.15) * mm, "end": v(-141.14, 71.15) * mm});
            skLineSegment(sketch, "E508", {"start": v(-141.14, 71.15) * mm, "end": v(-141.14, 88.93) * mm});
            skLineSegment(sketch, "E509", {"start": v(-141.14, 88.93) * mm, "end": v(-134.79, 88.93) * mm});
            skLineSegment(sketch, "E510", {"start": v(-134.79, 88.93) * mm, "end": v(-134.79, 82.58) * mm});
            skLineSegment(sketch, "E511", {"start": v(-134.79, 82.58) * mm, "end": v(-110.66, 82.58) * mm});
            skLineSegment(sketch, "E512", {"start": v(-110.66, 82.58) * mm, "end": v(-110.66, 99.09) * mm});
            skLineSegment(sketch, "E513", {"start": v(-156.38, 74.96) * mm, "end": v(-156.38, 92.74) * mm});
            skLineSegment(sketch, "E514", {"start": v(-186.86, 99.09) * mm, "end": v(-110.66, 99.09) * mm});
            skPoint(sketch, "E515", {"position": v(-148.76, 99.09) * mm});
            skLineSegment(sketch, "E516", {"start": v(-97.96, 50.83) * mm, "end": v(-67.48, 50.83) * mm});
            skLineSegment(sketch, "E517", {"start": v(-67.48, 50.83) * mm, "end": v(-67.48, 68.6) * mm});
            skLineSegment(sketch, "E518", {"start": v(-67.48, 68.6) * mm, "end": v(-73.83, 68.6) * mm});
            skLineSegment(sketch, "E519", {"start": v(-73.83, 68.6) * mm, "end": v(-73.83, 62.26) * mm});
            skLineSegment(sketch, "E520", {"start": v(-73.83, 62.26) * mm, "end": v(-97.96, 62.26) * mm});
            skLineSegment(sketch, "E521", {"start": v(-97.96, 62.26) * mm, "end": v(-97.96, 74.96) * mm});
            skLineSegment(sketch, "E522", {"start": v(-97.96, 74.96) * mm, "end": v(-67.48, 74.96) * mm});
            skLineSegment(sketch, "E523", {"start": v(-67.48, 92.74) * mm, "end": v(-73.83, 92.74) * mm});
            skLineSegment(sketch, "E524", {"start": v(-73.83, 92.74) * mm, "end": v(-73.83, 86.39) * mm});
            skLineSegment(sketch, "E525", {"start": v(-73.83, 86.39) * mm, "end": v(-97.96, 86.39) * mm});
            skLineSegment(sketch, "E526", {"start": v(-97.96, 86.39) * mm, "end": v(-97.96, 99.09) * mm});
            skLineSegment(sketch, "E527", {"start": v(-21.76, 47.02) * mm, "end": v(-52.24, 47.02) * mm});
            skLineSegment(sketch, "E528", {"start": v(-52.24, 47.02) * mm, "end": v(-52.24, 64.8) * mm});
            skLineSegment(sketch, "E529", {"start": v(-52.24, 64.8) * mm, "end": v(-45.89, 64.8) * mm});
            skLineSegment(sketch, "E530", {"start": v(-45.89, 64.8) * mm, "end": v(-45.89, 58.45) * mm});
            skLineSegment(sketch, "E531", {"start": v(-45.89, 58.45) * mm, "end": v(-21.76, 58.45) * mm});
            skLineSegment(sketch, "E532", {"start": v(-21.76, 58.45) * mm, "end": v(-21.76, 71.15) * mm});
            skLineSegment(sketch, "E533", {"start": v(-21.76, 71.15) * mm, "end": v(-52.24, 71.15) * mm});
            skLineSegment(sketch, "E534", {"start": v(-52.24, 71.15) * mm, "end": v(-52.24, 88.93) * mm});
            skLineSegment(sketch, "E535", {"start": v(-52.24, 88.93) * mm, "end": v(-45.89, 88.93) * mm});
            skLineSegment(sketch, "E536", {"start": v(-45.89, 88.93) * mm, "end": v(-45.89, 82.58) * mm});
            skLineSegment(sketch, "E537", {"start": v(-45.89, 82.58) * mm, "end": v(-21.76, 82.58) * mm});
            skLineSegment(sketch, "E538", {"start": v(-21.76, 82.58) * mm, "end": v(-21.76, 99.09) * mm});
            skLineSegment(sketch, "E539", {"start": v(-67.48, 74.96) * mm, "end": v(-67.48, 92.74) * mm});
            skLineSegment(sketch, "E540", {"start": v(-97.96, 99.09) * mm, "end": v(-21.76, 99.09) * mm});
            skPoint(sketch, "E541", {"position": v(-59.86, 99.09) * mm});
            skPoint(sketch, "E542", {"position": v(-282.1, 95.28) * mm});
            skSolve(sketch);
        }
        {
            var Q0;
            Q0=makeQuery(id+"F0.imprint","IMPRINT",FACE,{"disambiguationData":[TD([[makeQuery(id+"F0.imprint","IMPRINT",EDGE,{"derivedFrom":sQuery(id+"F0.wireOp",EDGE,"E0")}),1.0]])]});
            extrude(context, id + "F1", {"entities" : qUnion([Q0]), "depth" : 6.35 * mm});
        }
    });
